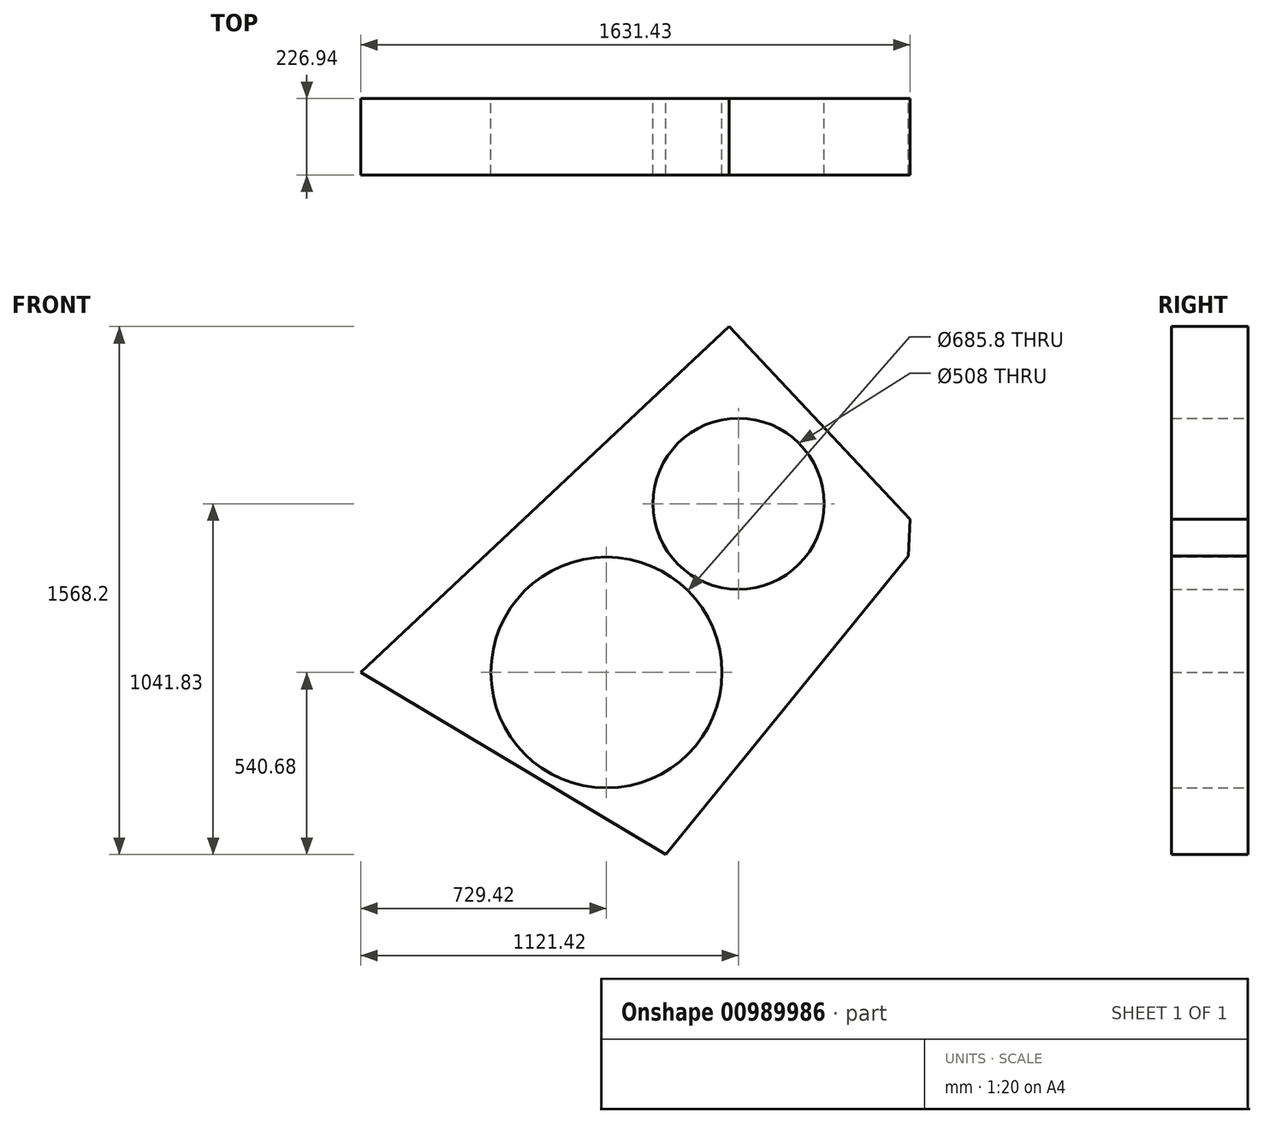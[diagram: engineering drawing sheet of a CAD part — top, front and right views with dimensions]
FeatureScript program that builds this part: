
annotation { "Feature Type Name" : "Feature", "Feature Type Description" : "" }
export const myFeature = defineFeature(function(context is Context, id is Id, definition is map)
    precondition{}
    {
        {
            var Q0;
            Q0=qCreatedBy(makeId("Front.planeOp"),FACE);
            var sketch = newSketch(context, id + "F0", { "sketchPlane" : qUnion([Q0])});
            skCircle(sketch, "E0", {"center": v(0, 0) * mm, "radius": 342.9 * mm});
            skCircle(sketch, "E1", {"center": v(392, 501.15) * mm, "radius": 254 * mm});
            skLineSegment(sketch, "E2", {"start": v(-729.42, 0) * mm, "end": v(364.2, 1027.52) * mm});
            skLineSegment(sketch, "E3", {"start": v(364.2, 1027.52) * mm, "end": v(364.2, 1027.52) * mm});
            skLineSegment(sketch, "E4", {"start": v(364.2, 1027.52) * mm, "end": v(902.01, 455.12) * mm});
            skLineSegment(sketch, "E5", {"start": v(902.01, 455.12) * mm, "end": v(896.17, 345.85) * mm});
            skLineSegment(sketch, "E6", {"start": v(896.17, 345.85) * mm, "end": v(175.95, -540.68) * mm});
            skLineSegment(sketch, "E7", {"start": v(175.95, -540.68) * mm, "end": v(-729.42, 0) * mm});
            skSolve(sketch);
        }
        {
            var Q0;
            Q0 = qSketchRegion(id + "F0", true);
            extrude(context, id + "F1", {"entities" : qUnion([Q0]), "depth" : 226.94 * mm, "offsetDistance" : 25.4 * mm});
        }
    });
